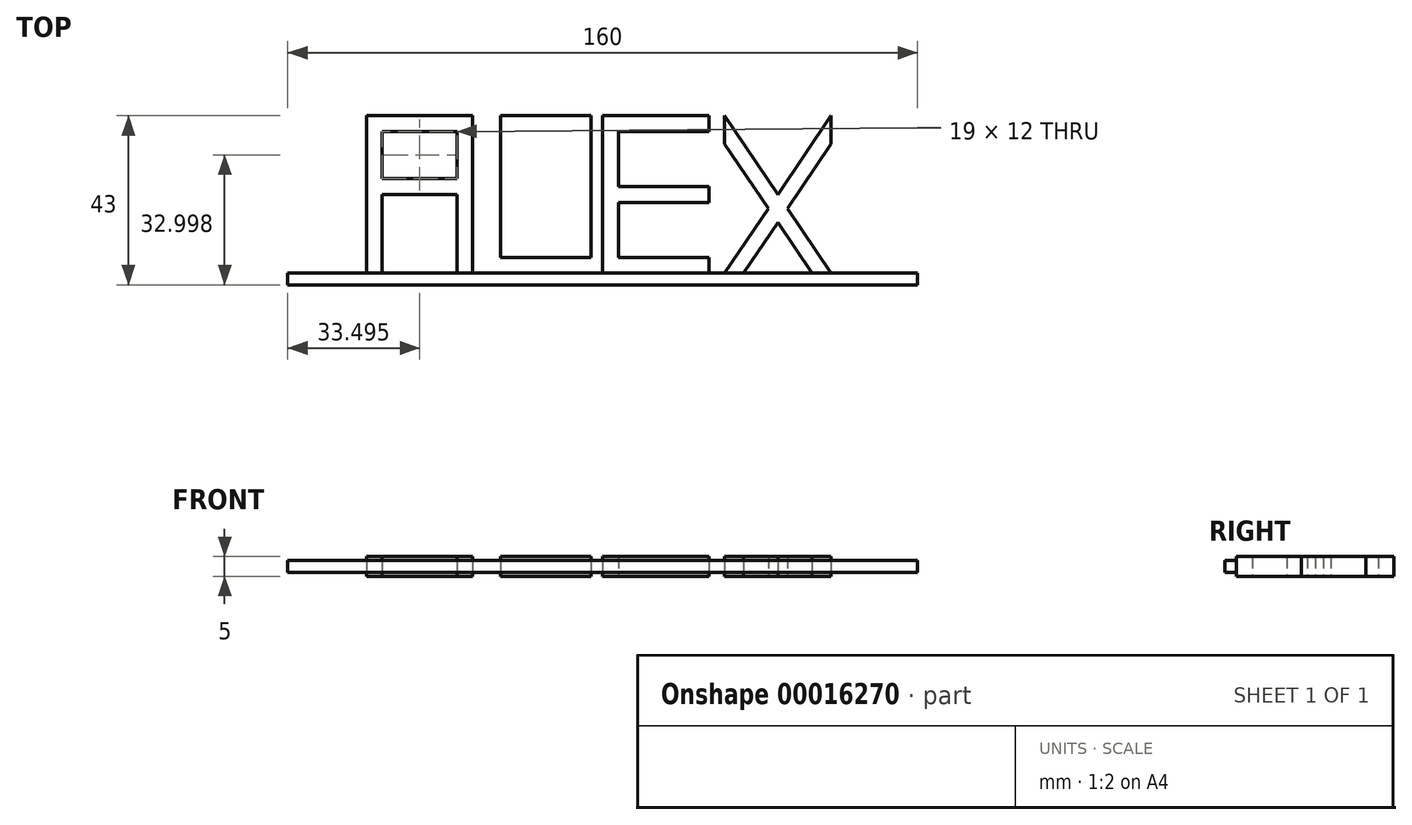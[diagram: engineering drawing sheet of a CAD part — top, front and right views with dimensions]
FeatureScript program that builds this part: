
annotation { "Feature Type Name" : "Feature", "Feature Type Description" : "" }
export const myFeature = defineFeature(function(context is Context, id is Id, definition is map)
    precondition{}
    {
        {
            var Q0;
            Q0=qCreatedBy(makeId("Top.planeOp"),FACE);
            var sketch = newSketch(context, id + "F0", { "sketchPlane" : qUnion([Q0])});
            skLineSegment(sketch, "E0.bottom", {"start": v(-79.84, -10.05) * mm, "end": v(80.16, -10.05) * mm});
            skLineSegment(sketch, "E0.top", {"start": v(-79.84, -13.05) * mm, "end": v(80.16, -13.05) * mm});
            skLineSegment(sketch, "E0.left", {"start": v(-79.84, -10.05) * mm, "end": v(-79.84, -13.05) * mm});
            skLineSegment(sketch, "E0.right", {"start": v(80.16, -10.05) * mm, "end": v(80.16, -13.05) * mm});
            skSolve(sketch);
        }
        {
            var Q0;
            Q0 = qSketchRegion(id + "F0", true);
            extrude(context, id + "F1", {"entities" : qUnion([Q0]), "endBound" : BoundingType.SYMMETRIC, "depth" : 3 * mm});
        }
        {
            var Q0;
            Q0=qCreatedBy(makeId("Top.planeOp"),FACE);
            var sketch = newSketch(context, id + "F2", { "sketchPlane" : qUnion([Q0])});
            skLineSegment(sketch, "E1.bottom", {"start": v(-59.84, 29.95) * mm, "end": v(-32.84, 29.95) * mm});
            skLineSegment(sketch, "E1.top", {"start": v(-59.84, -10.05) * mm, "end": v(-32.84, -10.05) * mm});
            skLineSegment(sketch, "E1.left", {"start": v(-59.84, 29.95) * mm, "end": v(-59.84, -10.05) * mm});
            skLineSegment(sketch, "E1.right", {"start": v(-32.84, 29.95) * mm, "end": v(-32.84, -10.05) * mm});
            skLineSegment(sketch, "E2.bottom", {"start": v(-55.84, 9.95) * mm, "end": v(-36.84, 9.95) * mm});
            skLineSegment(sketch, "E2.top", {"start": v(-55.84, -10.05) * mm, "end": v(-36.84, -10.05) * mm});
            skLineSegment(sketch, "E2.left", {"start": v(-55.84, 9.95) * mm, "end": v(-55.84, -10.05) * mm});
            skLineSegment(sketch, "E2.right", {"start": v(-36.84, 9.95) * mm, "end": v(-36.84, -10.05) * mm});
            skLineSegment(sketch, "E3.bottom", {"start": v(-55.84, 25.95) * mm, "end": v(-36.84, 25.95) * mm});
            skLineSegment(sketch, "E3.top", {"start": v(-55.84, 13.95) * mm, "end": v(-36.84, 13.95) * mm});
            skLineSegment(sketch, "E3.left", {"start": v(-55.84, 25.95) * mm, "end": v(-55.84, 13.95) * mm});
            skLineSegment(sketch, "E3.right", {"start": v(-36.84, 25.95) * mm, "end": v(-36.84, 13.95) * mm});
            skSolve(sketch);
        }
        {
            var Q0;
            Q0=makeQuery(id+"F2.imprint","IMPRINT",FACE,{"disambiguationData":[TD([[makeQuery(id+"F2.imprint","IMPRINT",EDGE,{"derivedFrom":sQuery(id+"F2.wireOp",EDGE,"E1.bottom")}),-1.0]])]});
            extrude(context, id + "F3", {"entities" : qUnion([Q0]), "operationType" : NewBodyOperationType.ADD, "endBound" : BoundingType.SYMMETRIC, "depth" : 5 * mm});
        }
        {
            var Q0;
            Q0=qCreatedBy(makeId("Top.planeOp"),FACE);
            var sketch = newSketch(context, id + "F4", { "sketchPlane" : qUnion([Q0])});
            skLineSegment(sketch, "E4.bottom", {"start": v(-29.84, 29.95) * mm, "end": v(-2.84, 29.95) * mm});
            skLineSegment(sketch, "E4.top", {"start": v(-29.84, -10.05) * mm, "end": v(-2.84, -10.05) * mm});
            skLineSegment(sketch, "E4.left", {"start": v(-29.84, 29.95) * mm, "end": v(-29.84, -10.05) * mm});
            skLineSegment(sketch, "E4.right", {"start": v(-2.84, 29.95) * mm, "end": v(-2.84, -10.05) * mm});
            skLineSegment(sketch, "E5.bottom", {"start": v(-25.84, 29.95) * mm, "end": v(-2.84, 29.95) * mm});
            skLineSegment(sketch, "E5.top", {"start": v(-25.84, -6.05) * mm, "end": v(-2.84, -6.05) * mm});
            skLineSegment(sketch, "E5.left", {"start": v(-25.84, 29.95) * mm, "end": v(-25.84, -6.05) * mm});
            skLineSegment(sketch, "E5.right", {"start": v(-2.84, 29.95) * mm, "end": v(-2.84, -6.05) * mm});
            skSolve(sketch);
        }
        {
            var Q0;
            Q0=makeQuery(id+"F4.imprint","IMPRINT",FACE,{"disambiguationData":[TD([[makeQuery(id+"F4.imprint","IMPRINT",EDGE,{"derivedFrom":sQuery(id+"F4.wireOp",EDGE,"E4.bottom")}),-1.0]])]});
            extrude(context, id + "F5", {"entities" : qUnion([Q0]), "operationType" : NewBodyOperationType.ADD, "endBound" : BoundingType.SYMMETRIC, "depth" : 5 * mm});
        }
        {
            var Q0;
            Q0=qCreatedBy(makeId("Top.planeOp"),FACE);
            var sketch = newSketch(context, id + "F6", { "sketchPlane" : qUnion([Q0])});
            skLineSegment(sketch, "E6.bottom", {"start": v(0.16, 29.95) * mm, "end": v(27.16, 29.95) * mm});
            skLineSegment(sketch, "E6.top", {"start": v(0.16, -10.05) * mm, "end": v(27.16, -10.05) * mm});
            skLineSegment(sketch, "E6.left", {"start": v(0.16, 29.95) * mm, "end": v(0.16, -10.05) * mm});
            skLineSegment(sketch, "E6.right", {"start": v(27.16, 29.95) * mm, "end": v(27.16, -10.05) * mm});
            skLineSegment(sketch, "E7.bottom", {"start": v(4.16, 7.95) * mm, "end": v(27.16, 7.95) * mm});
            skLineSegment(sketch, "E7.top", {"start": v(4.16, -6.05) * mm, "end": v(27.16, -6.05) * mm});
            skLineSegment(sketch, "E7.left", {"start": v(4.16, 7.95) * mm, "end": v(4.16, -6.05) * mm});
            skLineSegment(sketch, "E7.right", {"start": v(27.16, 7.95) * mm, "end": v(27.16, -6.05) * mm});
            skLineSegment(sketch, "E8.bottom", {"start": v(4.16, 25.95) * mm, "end": v(27.16, 25.95) * mm});
            skLineSegment(sketch, "E8.top", {"start": v(4.16, 11.95) * mm, "end": v(27.16, 11.95) * mm});
            skLineSegment(sketch, "E8.left", {"start": v(4.16, 25.95) * mm, "end": v(4.16, 11.95) * mm});
            skLineSegment(sketch, "E8.right", {"start": v(27.16, 25.95) * mm, "end": v(27.16, 11.95) * mm});
            skSolve(sketch);
        }
        {
            var Q0;
            {var subQ8=sQuery(id+"F6.wireOp",EDGE,"E6.bottom");Q0=makeQuery(id+"F6.imprint","IMPRINT",FACE,{"disambiguationData":[TD([[makeQuery(id+"F6.imprint","IMPRINT",EDGE,{"derivedFrom":subQ8}),-1.0]])]});}
            extrude(context, id + "F7", {"entities" : qUnion([Q0]), "operationType" : NewBodyOperationType.ADD, "endBound" : BoundingType.SYMMETRIC, "depth" : 5 * mm});
        }
        {
            var Q0;
            Q0=qCreatedBy(makeId("Top.planeOp"),FACE);
            var sketch = newSketch(context, id + "F8", { "sketchPlane" : qUnion([Q0])});
            skLineSegment(sketch, "E9.bottom", {"start": v(31.16, 29.95) * mm, "end": v(58.16, 29.95) * mm});
            skLineSegment(sketch, "E9.top", {"start": v(31.16, -10.05) * mm, "end": v(58.16, -10.05) * mm});
            skLineSegment(sketch, "E9.left", {"start": v(31.16, 29.95) * mm, "end": v(31.16, -10.05) * mm});
            skLineSegment(sketch, "E9.right", {"start": v(58.16, 29.95) * mm, "end": v(58.16, -10.05) * mm});
            skLineSegment(sketch, "E10", {"start": v(31.16, 29.95) * mm, "end": v(58.16, -10.05) * mm});
            skLineSegment(sketch, "E11", {"start": v(58.16, 29.95) * mm, "end": v(31.16, -10.05) * mm});
            skLineSegment(sketch, "E12", {"start": v(31.16, 22.8) * mm, "end": v(53.33, -10.05) * mm});
            skLineSegment(sketch, "E13", {"start": v(58.16, 22.8) * mm, "end": v(35.98, -10.05) * mm});
            skSolve(sketch);
        }
        {
            var Q0;
            {var subQ3=sQuery(id+"F8.wireOp",EDGE,"E10");var subQ5=sQuery(id+"F8.wireOp",EDGE,"E11");var subQ7=makeQuery(id+"F8.imprint","INTERSECT",VERTEX,{"derivedFrom":[subQ3,subQ5]});Q0=makeQuery(id+"F8.imprint","IMPRINT",FACE,{"disambiguationData":[TD([[makeQuery(id+"F8.imprint","IMPRINT",EDGE,{"disambiguationData":[TD([[subQ7,-1.0]])],"derivedFrom":subQ3}),-1.0]])]});}
            var Q1;
            {var subQ1=sQuery(id+"F8.wireOp",EDGE,"E10");var subQ5=sQuery(id+"F8.wireOp",EDGE,"E11");var subQ6=makeQuery(id+"F8.imprint","INTERSECT",VERTEX,{"derivedFrom":[subQ1,subQ5]});Q1=makeQuery(id+"F8.imprint","IMPRINT",FACE,{"disambiguationData":[TD([[makeQuery(id+"F8.imprint","IMPRINT",EDGE,{"disambiguationData":[TD([[subQ6,-1.0]])],"derivedFrom":subQ1}),1.0]])]});}
            var Q2;
            {var subQ1=sQuery(id+"F8.wireOp",EDGE,"E11");var subQ5=sQuery(id+"F8.wireOp",EDGE,"E10");var subQ6=makeQuery(id+"F8.imprint","INTERSECT",VERTEX,{"derivedFrom":[subQ5,subQ1]});Q2=makeQuery(id+"F8.imprint","IMPRINT",FACE,{"disambiguationData":[TD([[makeQuery(id+"F8.imprint","IMPRINT",EDGE,{"disambiguationData":[TD([[subQ6,-1.0]])],"derivedFrom":subQ1}),-1.0]])]});}
            var Q3;
            {var subQ1=sQuery(id+"F8.wireOp",EDGE,"E12");var subQ5=sQuery(id+"F8.wireOp",EDGE,"E11");var subQ6=makeQuery(id+"F8.imprint","INTERSECT",VERTEX,{"derivedFrom":[subQ5,subQ1]});Q3=makeQuery(id+"F8.imprint","IMPRINT",FACE,{"disambiguationData":[TD([[makeQuery(id+"F8.imprint","IMPRINT",EDGE,{"disambiguationData":[TD([[subQ6,-1.0]])],"derivedFrom":subQ1}),-1.0]])]});}
            var Q4;
            {var subQ1=sQuery(id+"F8.wireOp",EDGE,"E12");var subQ5=sQuery(id+"F8.wireOp",EDGE,"E9.top");var subQ6=makeQuery(id+"F8.imprint","INTERSECT",VERTEX,{"derivedFrom":[subQ5,subQ1]});Q4=makeQuery(id+"F8.imprint","IMPRINT",FACE,{"disambiguationData":[TD([[makeQuery(id+"F8.imprint","IMPRINT",EDGE,{"disambiguationData":[TD([[subQ6,1.0]])],"derivedFrom":subQ1}),1.0]])]});}
            extrude(context, id + "F9", {"entities" : qUnion([Q0, Q1, Q2, Q3, Q4]), "operationType" : NewBodyOperationType.ADD, "endBound" : BoundingType.SYMMETRIC, "depth" : 5 * mm});
        }
    });
